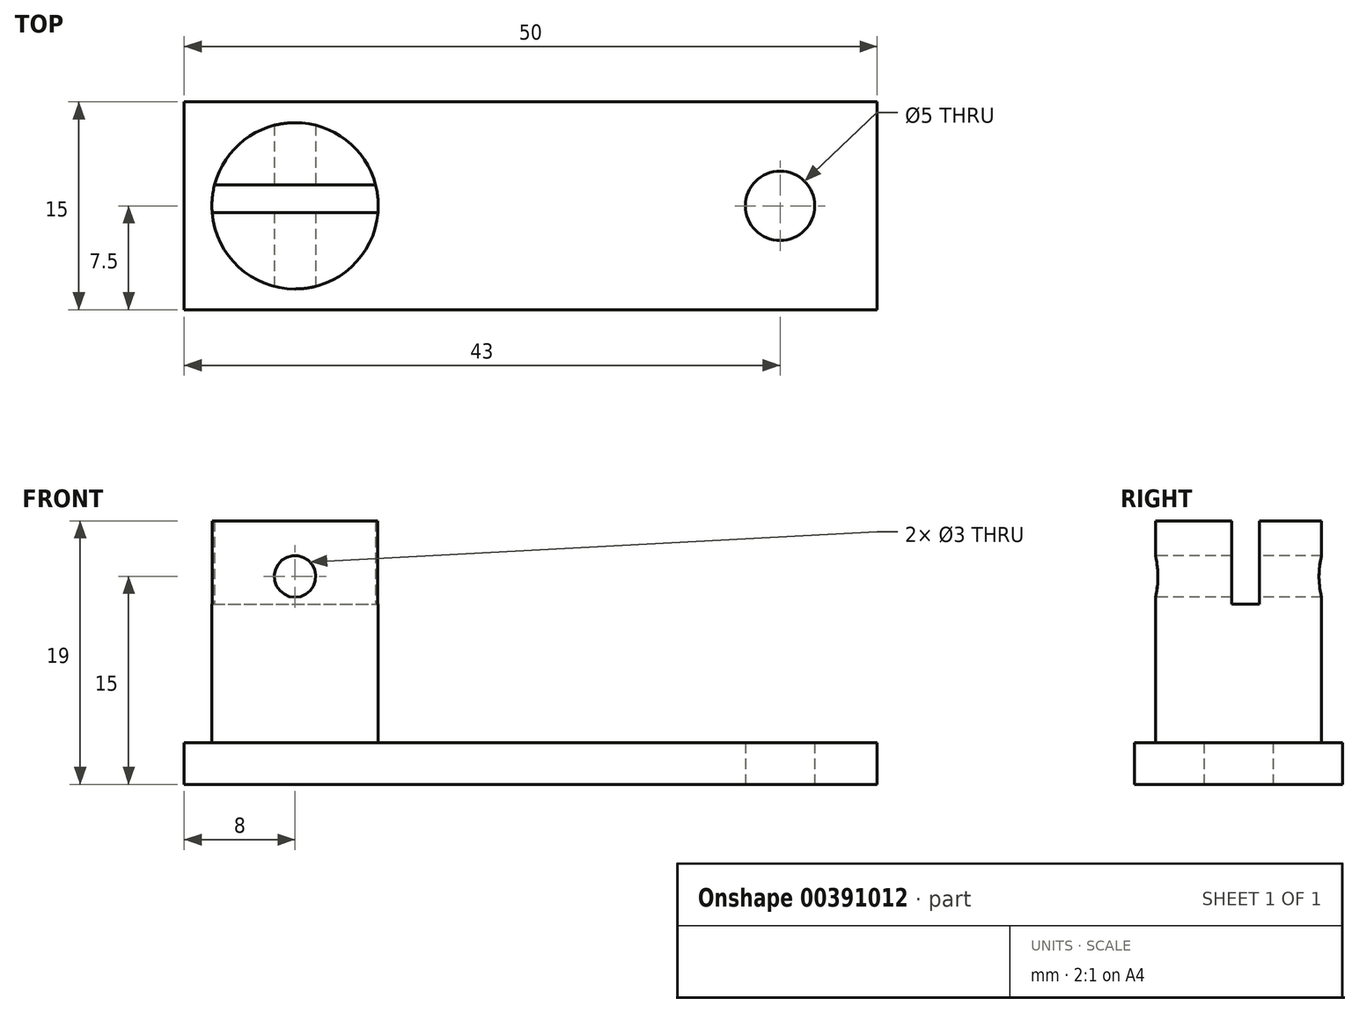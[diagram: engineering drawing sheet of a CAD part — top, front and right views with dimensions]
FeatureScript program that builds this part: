
annotation { "Feature Type Name" : "Feature", "Feature Type Description" : "" }
export const myFeature = defineFeature(function(context is Context, id is Id, definition is map)
    precondition{}
    {
        {
            var Q0;
            Q0=qCreatedBy(makeId("Top.planeOp"),FACE);
            var sketch = newSketch(context, id + "F0", { "sketchPlane" : qUnion([Q0])});
            skLineSegment(sketch, "E0", {"start": v(0, 0) * mm, "end": v(50, 0) * mm});
            skLineSegment(sketch, "E1", {"start": v(50, 0) * mm, "end": v(50, 15) * mm});
            skLineSegment(sketch, "E2", {"start": v(50, 15) * mm, "end": v(0, 15) * mm});
            skLineSegment(sketch, "E3", {"start": v(0, 15) * mm, "end": v(0, 0) * mm});
            skCircle(sketch, "E4", {"center": v(8, 7.5) * mm, "radius": 6 * mm});
            skCircle(sketch, "E5", {"center": v(43, 7.5) * mm, "radius": 2.5 * mm});
            skSolve(sketch);
        }
        {
            var Q0;
            Q0=makeQuery(id+"F0.imprint","IMPRINT",FACE,{"disambiguationData":[TD([[makeQuery(id+"F0.imprint","IMPRINT",EDGE,{"derivedFrom":sQuery(id+"F0.wireOp",EDGE,"E4")}),1.0]])]});
            var Q1;
            Q1=makeQuery(id+"F0.imprint","IMPRINT",FACE,{"disambiguationData":[TD([[makeQuery(id+"F0.imprint","IMPRINT",EDGE,{"derivedFrom":sQuery(id+"F0.wireOp",EDGE,"E0")}),1.0]])]});
            extrude(context, id + "F1", {"entities" : qUnion([Q0, Q1]), "depth" : 3 * mm});
        }
        {
            var Q0;
            Q0=qCreatedBy(makeId("Top.planeOp"),FACE);
            var sketch = newSketch(context, id + "F2", { "sketchPlane" : qUnion([Q0])});
            skCircle(sketch, "E6", {"center": v(8, 7.5) * mm, "radius": 6 * mm});
            skSolve(sketch);
        }
        {
            var Q0;
            Q0 = qSketchRegion(id + "F2", true);
            extrude(context, id + "F3", {"entities" : qUnion([Q0]), "operationType" : NewBodyOperationType.ADD, "depth" : 19 * mm});
        }
        {
            var Q0;
            Q0=makeQuery(id+"F3.opExtrude","CAP_FACE",FACE,{"disambiguationData":[OSD([sQuery(id+"F2.wireOp",EDGE,"E6")])],"isStart":false});
            cPlane(context, id + "F4", {"entities" : qUnion([Q0]), "cplaneType" : CPlaneType.OFFSET, "offset" : 0 * mm, "width" : 150 * mm, "height" : 150 * mm});
        }
        {
            var Q0;
            Q0=qCreatedBy(id+"F4.planeOp",FACE);
            var sketch = newSketch(context, id + "F5", { "sketchPlane" : qUnion([Q0])});
            skLineSegment(sketch, "E7", {"start": v(0, 0) * mm, "end": v(0, 8) * mm});
            skLineSegment(sketch, "E8.0", {"start": v(0, 7) * mm, "end": v(14.8, 7) * mm});
            skLineSegment(sketch, "E9.0", {"start": v(0, 9) * mm, "end": v(14.8, 9) * mm});
            skLineSegment(sketch, "E10", {"start": v(0, 7) * mm, "end": v(0, 9) * mm});
            skLineSegment(sketch, "E11", {"start": v(14.8, 9) * mm, "end": v(14.8, 7) * mm});
            skSolve(sketch);
        }
        {
            var Q0;
            {var subQ0=sQuery(id+"F5.wireOp",EDGE,"E8.0");Q0=makeQuery(id+"F5.imprint","IMPRINT",FACE,{"disambiguationData":[TD([[makeQuery(id+"F5.imprint","IMPRINT",EDGE,{"derivedFrom":subQ0}),1.0]])]});}
            var Q1;
            Q1=sQuery(id+"F5.wireOp",EDGE,"E9.0");
            var Q2;
            Q2=sQuery(id+"F5.wireOp",EDGE,"E8.0");
            var Q3;
            Q3=sQuery(id+"F5.wireOp",EDGE,"E11");
            var Q4;
            Q4=sQuery(id+"F5.wireOp",EDGE,"E10");
            extrude(context, id + "F6", {"entities" : qUnion([Q0]), "operationType" : NewBodyOperationType.REMOVE, "surfaceEntities" : qUnion([Q1, Q2, Q3, Q4]), "oppositeDirection" : true, "depth" : 6 * mm});
        }
        {
            var Q0;
            Q0=makeQuery(id+"F1.opExtrude","SWEPT_FACE",FACE,{"disambiguationData":[OSD([sQuery(id+"F0.wireOp",EDGE,"E0")])]});
            cPlane(context, id + "F7", {"entities" : qUnion([Q0]), "cplaneType" : CPlaneType.OFFSET, "offset" : 0 * mm, "width" : 150 * mm, "height" : 150 * mm});
        }
        {
            var Q0;
            Q0=qCreatedBy(id+"F7.planeOp",FACE);
            var sketch = newSketch(context, id + "F8", { "sketchPlane" : qUnion([Q0])});
            skLineSegment(sketch, "E12", {"start": v(0, 0) * mm, "end": v(8, 0) * mm});
            skLineSegment(sketch, "E13", {"start": v(8, 0) * mm, "end": v(8, 15) * mm});
            skCircle(sketch, "E14", {"center": v(8, 15) * mm, "radius": 1.5 * mm});
            skSolve(sketch);
        }
        {
            var Q0;
            Q0=makeQuery(id+"F8.imprint","IMPRINT",FACE,{"disambiguationData":[TD([[makeQuery(id+"F8.imprint","IMPRINT",EDGE,{"derivedFrom":sQuery(id+"F8.wireOp",EDGE,"E14")}),1.0]])]});
            var Q1;
            Q1=sQuery(id+"F8.wireOp",EDGE,"E14");
            extrude(context, id + "F9", {"entities" : qUnion([Q0]), "operationType" : NewBodyOperationType.REMOVE, "surfaceEntities" : qUnion([Q1]), "oppositeDirection" : true, "depth" : 25 * mm});
        }
    });
